# Revit family: P350153-031
name_source: partatom
category: Lighting Fixtures
revit_build: Autodesk Revit 2014 (Build: 20130308_1515(x64)
units: mm (PartAtom-declared; Revit-internal decimal feet)

## types (1)
- P350153-031
    Apparent Load = 60 VA
    Assembly Code = D5020200
    Connector Description = Lighting Connector
    Default Elevation = 48"
    Description = Immerse yourself in a home atmosphere primed for relaxation and inspired
thinking with the beautiful craftsmanship of this semi-flush mount. Savor
this fresh take on a classic light choice as your gaze traces graceful arms
and clean, crisp lines coated in a gorgeous black finish. Lightly seeded glass
shade rest in shiny pedestal light bases that add an unexpected, but welcomed dash of modern personality to this clean, traditional design
    Diameter = 13 3/4"
    Features = • Lightly seeded glass shade rest in shiny pedestal light bases that add an unexpected, but
welcomed dash of modern personality to this clean, traditional design.
• Savor this fresh take on a classic light choice as your gaze traces graceful arms and clean,
crisp lines coated in a gorgeous black finish.
• Immerse yourself in a home atmosphere primed for relaxation and inspired thinking with the
semi-flush mount’s beautiful craftmanship.
• Ideal for any hall, foyer, stairways, or kitchen.
• Perfect for transitional, rustic, farmhouse, or coastal settings.
• Measures 13-3/4-inch width by 11-7/8-inch height.
• Use three candelabra base bulb that is sold separately (60w max - LED or incandescent).
• Able to be fully dimmable with dimmable bulbs.
• Includes installation instructions and mounting hardware.
• Progress Lighting products are designed for exceptional quality, reliability, and functionality
    Fixture distribution = Direct
    Glass = Hubbell - Glass
    Height = 11 7/8"
    Housing Material = Paint - Hubbell - Textured Camera Black
    Lamp = LED
    Load Classification = Lighting
    Manufacturer = Progress Lighting
    Model = P350153-031
    Power Factor = 1
    Product Documentation Link = https://hubbellcdn.com
    Product Link = https://www.hubbell.com
    URL = https://www.hubbell.com
    Voltage = 120 V
    Warranty = 5 years Warranty
    Wattage Comments = 60W
    Watts = 60 W

## geometry (parser evidence)
native form markers: Sweep x4
no freeform markers — native parametric forms only
